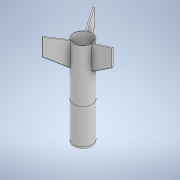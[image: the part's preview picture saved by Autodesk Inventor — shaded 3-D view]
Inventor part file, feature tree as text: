
AUTODESK INVENTOR PART (.ipt)
format: ipt  version: 2020.3 (Build 243373000, 373)  size: 275,456 bytes
history: native  units: mm
features: extrude x6, sketch x5, plane x2, chamfer x2, projected_geometry x2, pattern_circular x1, split x1
ambient origin geometry x8: Origin, YZ Plane, XZ Plane, XY Plane, X Axis, Y Axis, Z Axis, Center Point
bodies: Solid1 (feature_tree), Solid2 (feature_tree), Solid3 (feature_tree)
feature tree (19):
  sketch  "Sketch1"  dims[d0=50.0mm d1=51.8mm]
  extrude  "Extrusion1"  Depth=51.8mm
  extrude  "Extrusion2"  Depth=75.0mm TaperAngle=0.0deg
  extrude  "Extrusion4"  Depth=70.0mm
  plane  "Work Plane1"
  extrude  "Extrusion5"  Depth=50.0mm
  chamfer  "Chamfer1"  Distance=3.6mm
  chamfer  "Chamfer2"  Distance=175.0mm
  pattern_circular  "Circular Pattern3"  [2 undecoded]
  plane  "Work Plane2"
  split  "Split1"
  extrude  "Extrusion6"  [1 undecoded]
  extrude  "Extrusion7"  Depth=5.0mm TaperAngle=45.0deg
  sketch  "Sketch4"  dims[d2=53.6mm d3=75.0mm d4=180.0mm d5=0.0mm d6=0.0mm]
  projected_geometry  "Projected Loop1"
  sketch  "Sketch7"  dims[d21=9.930923mm d24=50.0mm]
  sketch  "Sketch8"  dims[d25=60.0mm d26=3.6mm d27=0.0mm d31=175.0mm d32=0.0mm d33=5.0mm d34=-145.0mm d35=50.0mm d36=51.8mm d37=53.6mm d38=5.0mm d39=5.0mm d40=0.0mm d41=1.8mm d42=2.0mm d43=45.0deg d44=1.8mm d45=2.0mm d46=45.0deg d47=30.0mm d48=360.0deg d50=-75.0mm d51=50.0mm d52=51.8mm d53=5.0mm d54=0.0mm d55=50.0mm d56=51.8mm d57=5.0mm d58=0.0mm d11=0.5mm d12=0.872665mm d13=0.5mm d14=0.872665mm]
  projected_geometry  "Project Cut Edges1"
  sketch  "Sketch5"  dims[d7=75.0mm d8=0.0mm d18=70.0mm]
note: 3 required parameter values undecoded (feature->parameter linkage not recoverable at this tier; creation-order binding heuristic only, values carry confidence <= 0.55)
